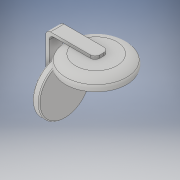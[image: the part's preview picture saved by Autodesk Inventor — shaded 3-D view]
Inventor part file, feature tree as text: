
AUTODESK INVENTOR PART (.ipt)
format: ipt  version: 2017 (Build 210142000, 142)  size: 232,960 bytes
history: native  units: in
note: dims shown in document units (in); Inventor stores cm internally (conversion verified against a paired STEP export)
features: sketch x8, fillet x7, extrude x6, plane x1
ambient origin geometry x8: Origin, YZ Plane, XZ Plane, XY Plane, X Axis, Y Axis, Z Axis, Center Point
bodies: Solid1 (feature_tree)
feature tree (22):
  extrude  "Extrusion1"  Depth=1.1875in
  fillet  "Fillet1"  Radius=0.625in
  fillet  "Fillet2"  Radius=0.3in
  extrude  "Extrusion2"  [1 undecoded]
  fillet  "Fillet3"  Radius=4.5in
  sketch  "Sketch3"  dims[d10=5.5in d11=0.0in d12=0.5in]
  plane  "Work Plane1"
  extrude  "Extrusion3"  Depth=0.5in
  extrude  "Extrusion4"  Depth=1.417in
  fillet  "Fillet4"  Radius=0.25in
  fillet  "Fillet5"  Radius=0.1in
  sketch  "Sketch6"
  sketch  "Sketch7"
  extrude  "Extrusion5"  Depth=0.1in
  fillet  "Fillet6"  [1 undecoded]
  extrude  "Extrusion6"  [1 undecoded]
  fillet  "Fillet7"  [1 undecoded]
  sketch  "Sketch1"  dims[d0=1.2in d1=0.0in d2=1.1875in d3=0.625in d4=0.3in d5=0.0in]
  sketch  "Sketch2"  dims[d6=0.5in d7=-0.5in d8=4.5in d9=0.0in]
  sketch  "Sketch4"  dims[d13=0.5in d14=1.417in d15=0.25in d16=0.0in d17=0.1in]
  sketch  "Sketch5"  dims[d18=0.7in d19=0.0in d20=0.1in]
  sketch  "Sketch8"
note: 4 required parameter values undecoded (feature->parameter linkage not recoverable at this tier; creation-order binding heuristic only, values carry confidence <= 0.55)
